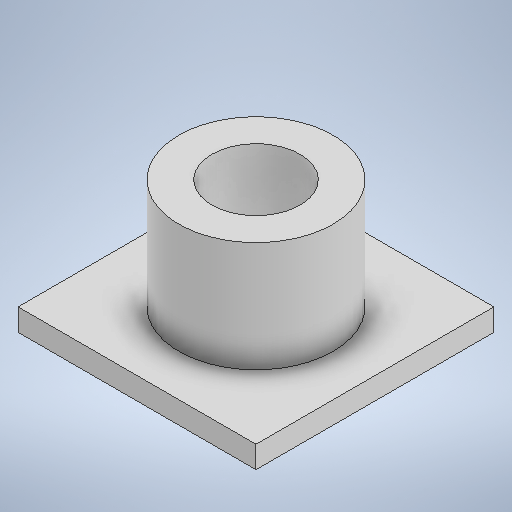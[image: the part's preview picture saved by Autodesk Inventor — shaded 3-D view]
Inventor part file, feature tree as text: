
AUTODESK INVENTOR PART (.ipt)
format: ipt  version: 2025 (Build 290162000, 162)  size: 235,520 bytes
history: native  units: mm
features: extrude x2, other x1, sketch x1
ambient origin geometry x8: Origin, YZ Plane, XZ Plane, XY Plane, X Axis, Y Axis, Z Axis, Center Point
bodies: Body1 (feature_tree)
feature tree (4):
  other  "Bryła1"
  sketch  "Szkic1"
  extrude  "Wyciągnięcie proste1"  Depth=20.0mm
  extrude  "Wyciągnięcie proste2"  Depth=54.0mm
